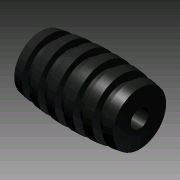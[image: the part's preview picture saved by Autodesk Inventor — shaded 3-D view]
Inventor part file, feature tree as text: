
AUTODESK INVENTOR PART (.ipt)
format: ipt  version: 2011 (Build 150239000, 239)  size: 150,528 bytes
history: native  units: in
note: dims shown in document units (in); Inventor stores cm internally (conversion verified against a paired STEP export)
features: revolve x1, sketch x1
ambient origin geometry x8: Origin, YZ Plane, XZ Plane, XY Plane, X Axis, Y Axis, Z Axis, Center Point
bodies: Solid1 (feature_tree)
feature tree (2):
  revolve  "Revolution1"  [1 undecoded]
  sketch  "Sketch1"  dims[d0=1.4in d1=0.25in d2=0.25in d3=3.77in d4=0.125in d5=90.0deg d7=0.125in d10=0.1291in d11=0.125in d13=0.1291in d16=0.1291in d18=0.1291in d19=0.6375in d20=0.125in d21=0.125in d22=0.125in d23=0.0925in d24=0.0925in d25=0.0925in d26=0.0925in d27=0.0925in d28=0.3046in d29=0.3347in d30=0.3475in]
note: 1 required parameter value undecoded (feature->parameter linkage not recoverable at this tier; creation-order binding heuristic only, values carry confidence <= 0.55)
